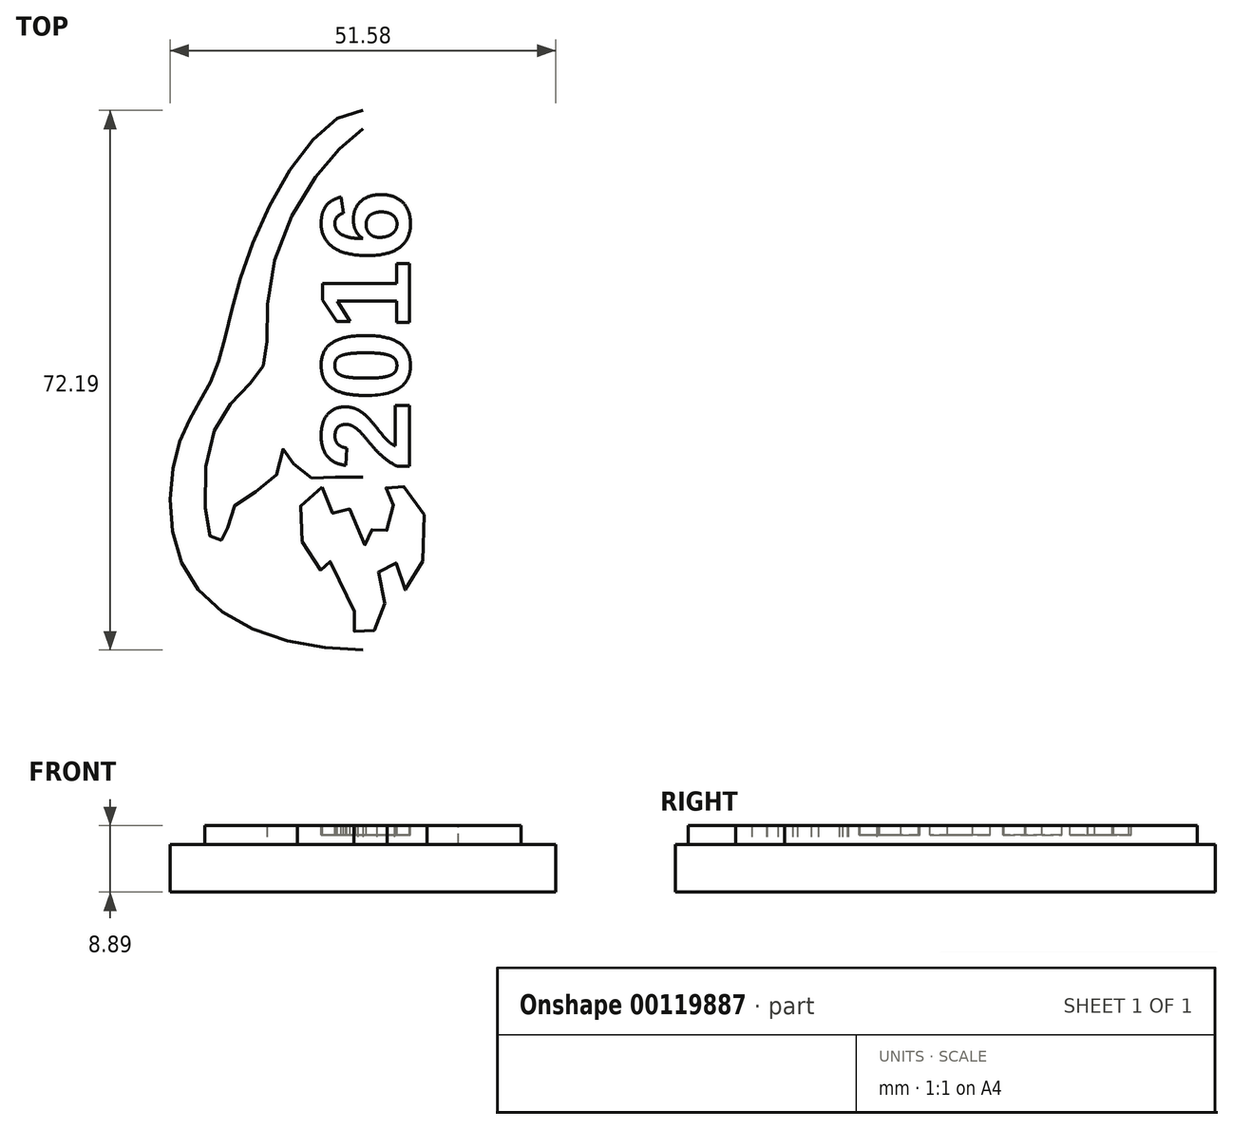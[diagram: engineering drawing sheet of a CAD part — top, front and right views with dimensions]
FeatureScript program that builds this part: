
annotation { "Feature Type Name" : "Feature", "Feature Type Description" : "" }
export const myFeature = defineFeature(function(context is Context, id is Id, definition is map)
    precondition{}
    {
        {
            var Q0;
            Q0=qCreatedBy(makeId("Top.planeOp"),FACE);
            var sketch = newSketch(context, id + "F0", { "sketchPlane" : qUnion([Q0])});
            skFitSpline(sketch, "E0", {"points": [v(0, 34.76) * mm, v(-15.24, 15.65) * mm, v(-20, -0.83) * mm, v(-24.62, -9.9) * mm, v(-22.8, -28.36) * mm, v(0, -37.43) * mm], "startDerivative": vector(-77.92, 0) * mm, "endDerivative": vector(116.72, 0) * mm});
            skLineSegment(sketch, "E1", {"start": v(0, 34.76) * mm, "end": v(0, -37.43) * mm});
            skSolve(sketch);
        }
        {
            var Q0;
            Q0 = qSketchRegion(id + "F0", true);
            extrude(context, id + "F1", {"entities" : qUnion([Q0]), "oppositeDirection" : true, "depth" : 6.35 * mm});
        }
        {
            var Q0;
            Q0=makeQuery(id+"F1.opExtrude","CAP_FACE",FACE,{"disambiguationData":[OSD([sQuery(id+"F0.wireOp",EDGE,"E0"),sQuery(id+"F0.wireOp",EDGE,"E1")])],"isStart":true});
            var sketch = newSketch(context, id + "F2", { "sketchPlane" : qUnion([Q0])});
            skFitSpline(sketch, "E2", {"points": [v(0, 32.34) * mm, v(-5.74, 26.64) * mm, v(-12.25, 12.95) * mm, v(-12.86, 2.49) * mm, v(-14.06, -0.66) * mm, v(-17.67, -4.43) * mm, v(-20.85, -11.65) * mm, v(-20.6, -21.63) * mm, v(-19.76, -22.8) * mm, v(-18.5, -22.47) * mm, v(-18.09, -20.87) * mm, v(-16.32, -17.18) * mm, v(-11.88, -14.67) * mm, v(-10.54, -10.47) * mm, v(-8.36, -13.74) * mm, v(-5.17, -14.33) * mm, v(0, -14.28) * mm], "startDerivative": vector(-72.01, -60.3) * mm, "endDerivative": vector(90.34, 4.61) * mm});
            skLineSegment(sketch, "E3", {"start": v(0, 32.34) * mm, "end": v(0, -14.28) * mm});
            skSolve(sketch);
        }
        {
            var Q0;
            Q0 = qSketchRegion(id + "F2", true);
            extrude(context, id + "F3", {"entities" : qUnion([Q0]), "operationType" : NewBodyOperationType.ADD, "depth" : 2.54 * mm});
        }
        {
            var Q0;
            Q0=makeQuery(id+"F1.opExtrude","SWEPT_BODY",BODY,{"disambiguationData":[OSD([sQuery(id+"F0.wireOp",EDGE,"E0"),sQuery(id+"F0.wireOp",EDGE,"E1")])]});
            var Q1;
            Q1=makeQuery(id+"F3.boolean.opBoolean","MERGE",FACE,{"derivedFrom":[makeQuery(id+"F1.opExtrude","SWEPT_FACE",FACE,{"disambiguationData":[OSD([sQuery(id+"F0.wireOp",EDGE,"E1")])]}),makeQuery(id+"F3.opExtrude","SWEPT_FACE",FACE,{"disambiguationData":[OSD([sQuery(id+"F2.wireOp",EDGE,"E3")])]})]});
            mirror(context, id + "F4", {"operationType" : NewBodyOperationType.ADD, "entities" : qUnion([Q0]), "mirrorPlane" : qUnion([Q1])});
        }
        {
            var Q0;
            {var subQ0=makeQuery(id+"F1.opExtrude","CAP_FACE",FACE,{"disambiguationData":[OSD([sQuery(id+"F0.wireOp",EDGE,"E0"),sQuery(id+"F0.wireOp",EDGE,"E1")])],"isStart":true});Q0=makeQuery(id+"F4.boolean.opBoolean","MERGE",FACE,{"derivedFrom":[subQ0,makeQuery(id+"F4.opPattern","COPY",FACE,{"derivedFrom":subQ0,"instanceName":"1"})]});}
            var sketch = newSketch(context, id + "F5", { "sketchPlane" : qUnion([Q0])});
            skFitSpline(sketch, "E4", {"points": [v(-5.47, -15.63) * mm, v(-8.63, -19.07) * mm, v(-6.66, -25.39) * mm, v(-4.82, -27.09) * mm, v(-4.17, -25.26) * mm, v(-1.95, -31.27) * mm, v(-0.68, -33.04) * mm, v(-1.03, -35.58) * mm, v(3.15, -33.1) * mm, v(1.84, -28.13) * mm, v(4.06, -25.26) * mm, v(5.53, -29.3) * mm, v(8.5, -23.16) * mm, v(5.9, -15.84) * mm, v(3.28, -15.32) * mm, v(3.41, -16.89) * mm, v(4.2, -18.72) * mm, v(2.63, -21.73) * mm, v(1.32, -21.17) * mm, v(0.54, -23.69) * mm, v(-2.08, -18.33) * mm, v(-3.9, -19.24) * mm, v(-5.47, -15.63) * mm]});
            skSolve(sketch);
        }
        {
            var Q0;
            Q0=makeQuery(id+"F5.imprint","IMPRINT",FACE,{"disambiguationData":[TD([[makeQuery(id+"F5.imprint","IMPRINT",EDGE,{"derivedFrom":sQuery(id+"F5.wireOp",EDGE,"E4")}),1.0]])]});
            var Q1;
            Q1=sQuery(id+"F5.wireOp",EDGE,"E4");
            extrude(context, id + "F6", {"entities" : qUnion([Q0]), "operationType" : NewBodyOperationType.ADD, "surfaceEntities" : qUnion([Q1]), "depth" : 2.54 * mm});
        }
        {
            var Q0;
            {var subQ0=makeQuery(id+"F3.opExtrude","CAP_FACE",FACE,{"disambiguationData":[OSD([sQuery(id+"F2.wireOp",EDGE,"E2"),sQuery(id+"F2.wireOp",EDGE,"E3")])],"isStart":false});Q0=makeQuery(id+"F4.boolean.opBoolean","MERGE",FACE,{"derivedFrom":[subQ0,makeQuery(id+"F4.opPattern","COPY",FACE,{"derivedFrom":subQ0,"instanceName":"1"})]});}
            var sketch = newSketch(context, id + "F7", { "sketchPlane" : qUnion([Q0])});
            skLineSegment(sketch, "E5", {"start": v(6.21, -2.22) * mm, "end": v(6.21, 4.8) * mm});
            skText(sketch, "E6", { "text": "2016", "fontName": "Arimo-Bold.ttf"});
            const initialGuessF7  = {"E6": [0.00621, -0.01342, 0, 1, 0.01215]};
            skSetInitialGuess(sketch, initialGuessF7);
            skSolve(sketch);
        }
        {
            var Q0;
            Q0 = qSketchRegion(id + "F7", true);
            extrude(context, id + "F8", {"entities" : qUnion([Q0]), "operationType" : NewBodyOperationType.REMOVE, "oppositeDirection" : true, "depth" : 1.27 * mm});
        }
    });
